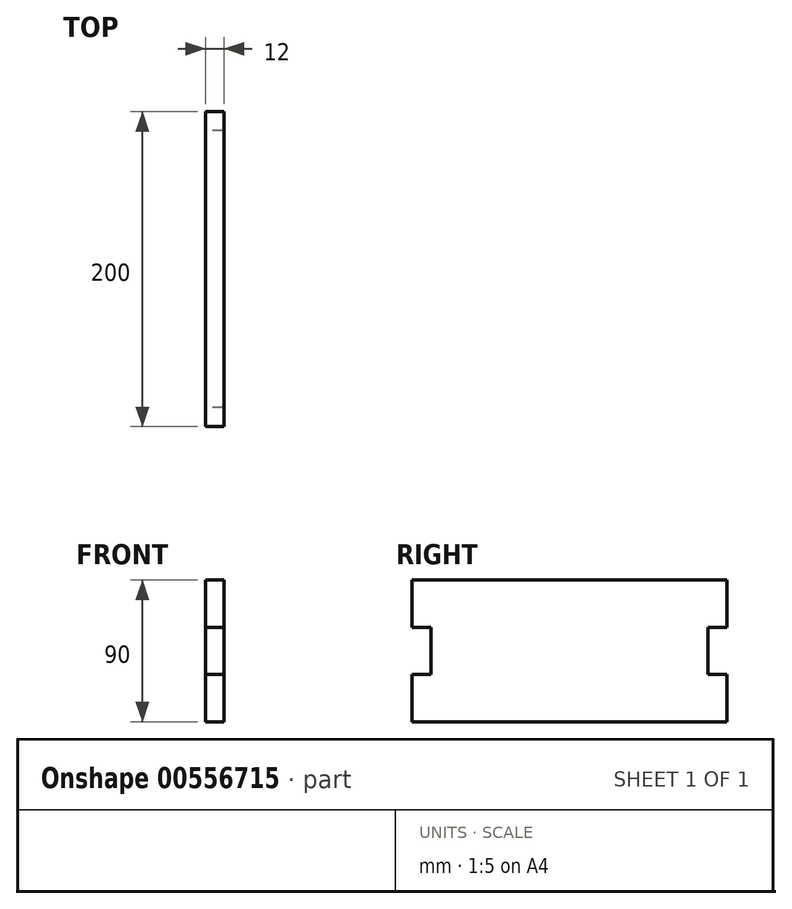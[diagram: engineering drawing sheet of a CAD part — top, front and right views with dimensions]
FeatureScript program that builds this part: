
annotation { "Feature Type Name" : "Feature", "Feature Type Description" : "" }
export const myFeature = defineFeature(function(context is Context, id is Id, definition is map)
    precondition{}
    {
        {
            var Q0;
            Q0=qCreatedBy(makeId("Right.planeOp"),FACE);
            var sketch = newSketch(context, id + "F0", { "sketchPlane" : qUnion([Q0])});
            skLineSegment(sketch, "E0", {"start": v(0, 0) * mm, "end": v(0, 30) * mm});
            skLineSegment(sketch, "E1", {"start": v(0, 30) * mm, "end": v(12, 30) * mm});
            skLineSegment(sketch, "E2", {"start": v(12, 30) * mm, "end": v(12, 60) * mm});
            skLineSegment(sketch, "E3", {"start": v(12, 60) * mm, "end": v(0, 60) * mm});
            skLineSegment(sketch, "E4", {"start": v(0, 60) * mm, "end": v(0, 90) * mm});
            skLineSegment(sketch, "E5", {"start": v(0, 90) * mm, "end": v(100, 90) * mm});
            skLineSegment(sketch, "E6", {"start": v(100, 90) * mm, "end": v(100, 0) * mm, "construction": true});
            skLineSegment(sketch, "E7", {"start": v(100, 0) * mm, "end": v(0, 0) * mm});
            skLineSegment(sketch, "E8.MirrorCS", {"start": v(200, 30) * mm, "end": v(188, 30) * mm});
            skLineSegment(sketch, "E9.MirrorCS", {"start": v(188, 30) * mm, "end": v(188, 60) * mm});
            skLineSegment(sketch, "E10.MirrorCS", {"start": v(200, 60) * mm, "end": v(200, 90) * mm});
            skLineSegment(sketch, "E11.MirrorCS", {"start": v(200, 0) * mm, "end": v(200, 30) * mm});
            skLineSegment(sketch, "E12.MirrorCS", {"start": v(200, 90) * mm, "end": v(100, 90) * mm});
            skLineSegment(sketch, "E13.MirrorCS", {"start": v(188, 60) * mm, "end": v(200, 60) * mm});
            skLineSegment(sketch, "E14.MirrorCS", {"start": v(100, 0) * mm, "end": v(200, 0) * mm});
            skSolve(sketch);
        }
        {
            var Q0;
            Q0=makeQuery(id+"F0.imprint","IMPRINT",FACE,{"disambiguationData":[TD([[makeQuery(id+"F0.imprint","IMPRINT",EDGE,{"derivedFrom":sQuery(id+"F0.wireOp",EDGE,"E0")}),-1.0]])]});
            extrude(context, id + "F1", {"entities" : qUnion([Q0]), "depth" : 12 * mm, "offsetDistance" : 25 * mm, "symmetric" : true});
        }
    });
